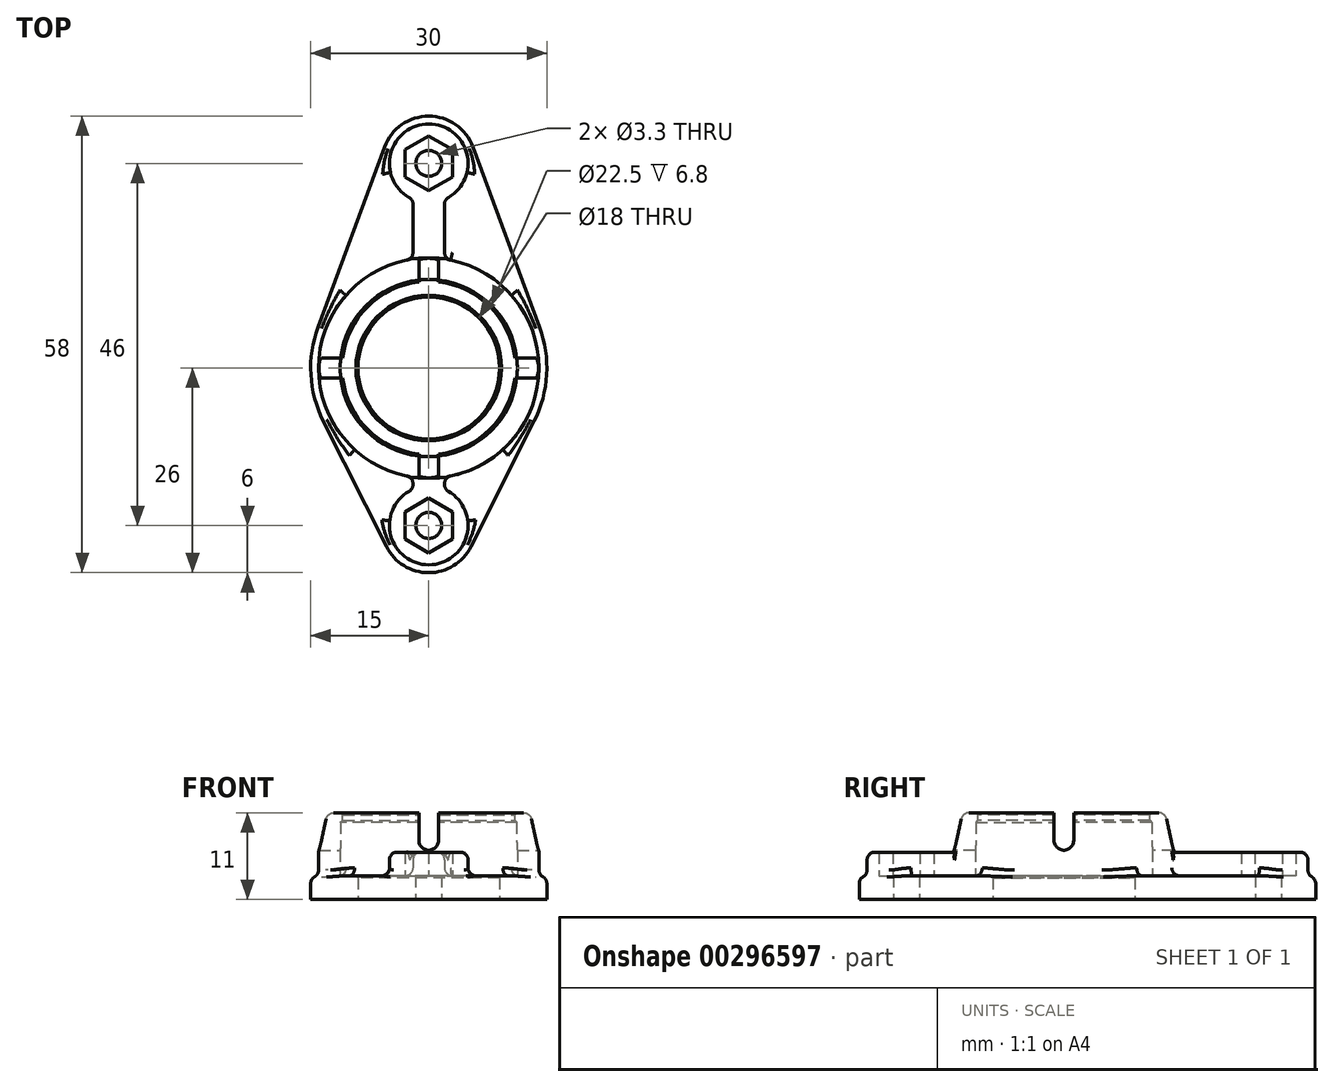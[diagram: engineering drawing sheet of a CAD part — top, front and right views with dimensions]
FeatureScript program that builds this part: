
annotation { "Feature Type Name" : "Feature", "Feature Type Description" : "" }
export const myFeature = defineFeature(function(context is Context, id is Id, definition is map)
    precondition{}
    {
        {
            var Q0;
            Q0=qCreatedBy(makeId("Top.planeOp"),FACE);
            var sketch = newSketch(context, id + "F0", { "sketchPlane" : qUnion([Q0])});
            skCircle(sketch, "E0", {"center": v(0, 0) * mm, "radius": 9 * mm});
            skArc(sketch, "E1", {"start": v(-14.07, 5.2) * mm, "mid": v(-14.98, -0.85) * mm, "end": v(-13.4, -6.75) * mm});
            skLineSegment(sketch, "E2", {"start": v(0, 0) * mm, "end": v(0, -20) * mm, "construction": true});
            skCircle(sketch, "E3", {"center": v(0, -20) * mm, "radius": 1.65 * mm});
            skLineSegment(sketch, "E4", {"start": v(0, 0) * mm, "end": v(0, 26) * mm, "construction": true});
            skCircle(sketch, "E5", {"center": v(0, 26) * mm, "radius": 1.65 * mm});
            skArc(sketch, "E6", {"start": v(5.63, 28.08) * mm, "mid": v(0, 32) * mm, "end": v(-5.63, 28.08) * mm});
            skArc(sketch, "E7", {"start": v(-5.36, -22.7) * mm, "mid": v(0, -26) * mm, "end": v(5.36, -22.7) * mm});
            skLineSegment(sketch, "E8", {"start": v(-5.63, 28.08) * mm, "end": v(-14.07, 5.2) * mm});
            skLineSegment(sketch, "E9", {"start": v(-13.4, -6.75) * mm, "end": v(-5.36, -22.7) * mm});
            skLineSegment(sketch, "E10", {"start": v(5.36, -22.7) * mm, "end": v(13.4, -6.75) * mm});
            skLineSegment(sketch, "E11", {"start": v(5.63, 28.08) * mm, "end": v(14.07, 5.2) * mm});
            skArc(sketch, "E12.trimOffspring", {"start": v(13.4, -6.75) * mm, "mid": v(14.98, -0.85) * mm, "end": v(14.07, 5.2) * mm});
            skSolve(sketch);
        }
        {
            var Q0;
            Q0=qSketchRegion(id+"F0",true);
            extrude(context, id + "F1", {"entities" : qUnion([Q0]), "depth" : 3 * mm});
        }
        {
            var Q0;
            Q0=makeQuery(id+"F1.opExtrude","CAP_FACE",FACE,{"disambiguationData":[OSD([sQuery(id+"F0.wireOp",EDGE,"E0"),sQuery(id+"F0.wireOp",EDGE,"E1"),sQuery(id+"F0.wireOp",EDGE,"E3"),sQuery(id+"F0.wireOp",EDGE,"E5"),sQuery(id+"F0.wireOp",EDGE,"E6"),sQuery(id+"F0.wireOp",EDGE,"E7"),sQuery(id+"F0.wireOp",EDGE,"E8"),sQuery(id+"F0.wireOp",EDGE,"E9"),sQuery(id+"F0.wireOp",EDGE,"E10"),sQuery(id+"F0.wireOp",EDGE,"E11"),sQuery(id+"F0.wireOp",EDGE,"E12.trimOffspring")])],"isStart":false});
            var sketch = newSketch(context, id + "F2", { "sketchPlane" : qUnion([Q0])});
            skArc(sketch, "E13", {"start": v(2.5, 21.67) * mm, "mid": v(0, 31) * mm, "end": v(-2.5, 21.67) * mm});
            skArc(sketch, "E14", {"start": v(-2.5, -15.67) * mm, "mid": v(0, -25) * mm, "end": v(2.5, -15.67) * mm});
            skCircle(sketch, "E15", {"center": v(0, 0) * mm, "radius": 11.25 * mm});
            skArc(sketch, "E16", {"start": v(-2.8, 13.72) * mm, "mid": v(-14, 0) * mm, "end": v(-2.8, -13.72) * mm});
            skLineSegment(sketch, "E17", {"start": v(0, 26) * mm, "end": v(0, 0) * mm, "construction": true});
            skLineSegment(sketch, "E18", {"start": v(0, -20) * mm, "end": v(0, 0) * mm, "construction": true});
            skLineSegment(sketch, "E19.0", {"start": v(2, -14.8) * mm, "end": v(2, -14.7) * mm});
            skLineSegment(sketch, "E20.0", {"start": v(-2, -14.8) * mm, "end": v(-2, -14.7) * mm});
            skLineSegment(sketch, "E21.0", {"start": v(-2, 20.8) * mm, "end": v(-2, 14.7) * mm});
            skLineSegment(sketch, "E22.0", {"start": v(2, 20.8) * mm, "end": v(2, 14.7) * mm});
            skArc(sketch, "E23.trimOffspring", {"start": v(2.8, -13.72) * mm, "mid": v(14, 0) * mm, "end": v(2.8, 13.72) * mm});
            skPoint(sketch, "E24.visualSharp", {"position": v(2, 13.86) * mm});
            skArc(sketch, "E24.filletArc", {"start": v(2, 14.7) * mm, "mid": v(2.23, 14.06) * mm, "end": v(2.8, 13.72) * mm});
            skPoint(sketch, "E25.visualSharp", {"position": v(2, -13.86) * mm});
            skArc(sketch, "E25.filletArc", {"start": v(2.8, -13.72) * mm, "mid": v(2.23, -14.06) * mm, "end": v(2, -14.7) * mm});
            skPoint(sketch, "E26.visualSharp", {"position": v(2, -15.42) * mm});
            skArc(sketch, "E26.filletArc", {"start": v(2, -14.8) * mm, "mid": v(2.13, -15.3) * mm, "end": v(2.5, -15.67) * mm});
            skPoint(sketch, "E27.visualSharp", {"position": v(-2, -15.42) * mm});
            skArc(sketch, "E27.filletArc", {"start": v(-2.5, -15.67) * mm, "mid": v(-2.13, -15.3) * mm, "end": v(-2, -14.8) * mm});
            skPoint(sketch, "E28.visualSharp", {"position": v(-2, -13.86) * mm});
            skArc(sketch, "E28.filletArc", {"start": v(-2, -14.7) * mm, "mid": v(-2.23, -14.06) * mm, "end": v(-2.8, -13.72) * mm});
            skPoint(sketch, "E29.visualSharp", {"position": v(2, 21.42) * mm});
            skArc(sketch, "E29.filletArc", {"start": v(2.5, 21.67) * mm, "mid": v(2.13, 21.3) * mm, "end": v(2, 20.8) * mm});
            skPoint(sketch, "E30.visualSharp", {"position": v(-2, 21.42) * mm});
            skArc(sketch, "E30.filletArc", {"start": v(-2, 20.8) * mm, "mid": v(-2.13, 21.3) * mm, "end": v(-2.5, 21.67) * mm});
            skPoint(sketch, "E31.visualSharp", {"position": v(-2, 13.86) * mm});
            skArc(sketch, "E31.filletArc", {"start": v(-2.8, 13.72) * mm, "mid": v(-2.23, 14.06) * mm, "end": v(-2, 14.7) * mm});
            skCircle(sketch, "E32.cCircle", {"center": v(0, 26) * mm, "radius": 3 * mm, "construction": true});
            skLineSegment(sketch, "E32.0", {"start": v(3, 27.73) * mm, "end": v(3, 24.27) * mm});
            skLineSegment(sketch, "E32.1", {"start": v(3, 24.27) * mm, "end": v(0, 22.54) * mm});
            skLineSegment(sketch, "E32.2", {"start": v(0, 22.54) * mm, "end": v(-3, 24.27) * mm});
            skLineSegment(sketch, "E32.3", {"start": v(-3, 24.27) * mm, "end": v(-3, 27.73) * mm});
            skLineSegment(sketch, "E32.4", {"start": v(-3, 27.73) * mm, "end": v(0, 29.46) * mm});
            skLineSegment(sketch, "E32.5", {"start": v(0, 29.46) * mm, "end": v(3, 27.73) * mm});
            skPoint(sketch, "E32.0.midPoint", {"position": v(3, 26) * mm});
            skCircle(sketch, "E33.cCircle", {"center": v(0, -20) * mm, "radius": 3 * mm, "construction": true});
            skLineSegment(sketch, "E33.0", {"start": v(3, -18.27) * mm, "end": v(3, -21.73) * mm});
            skLineSegment(sketch, "E33.1", {"start": v(3, -21.73) * mm, "end": v(0, -23.46) * mm});
            skLineSegment(sketch, "E33.2", {"start": v(0, -23.46) * mm, "end": v(-3, -21.73) * mm});
            skLineSegment(sketch, "E33.3", {"start": v(-3, -21.73) * mm, "end": v(-3, -18.27) * mm});
            skLineSegment(sketch, "E33.4", {"start": v(-3, -18.27) * mm, "end": v(0, -16.54) * mm});
            skLineSegment(sketch, "E33.5", {"start": v(0, -16.54) * mm, "end": v(3, -18.27) * mm});
            skPoint(sketch, "E33.0.midPoint", {"position": v(3, -20) * mm});
            skSolve(sketch);
        }
        {
            var Q0;
            Q0=qSketchRegion(id+"F2",true);
            extrude(context, id + "F3", {"entities" : qUnion([Q0]), "operationType" : NewBodyOperationType.ADD, "depth" : 3 * mm});
        }
        {
            var Q0;
            Q0=makeQuery(id+"F3.opExtrude","CAP_FACE",FACE,{"disambiguationData":[OSD([sQuery(id+"F2.wireOp",EDGE,"ErkzImGW-wcGA-vscJ-pKRm-jUK9ljDqNzHm"),sQuery(id+"F2.wireOp",EDGE,"E13"),sQuery(id+"F2.wireOp",EDGE,"mcYN25WA-hLG2-lxEH-biPS-aZDlqV3Zxszz"),sQuery(id+"F2.wireOp",EDGE,"E14"),sQuery(id+"F2.wireOp",EDGE,"E15"),sQuery(id+"F2.wireOp",EDGE,"E16"),sQuery(id+"F2.wireOp",EDGE,"E19.0"),sQuery(id+"F2.wireOp",EDGE,"E20.0"),sQuery(id+"F2.wireOp",EDGE,"E21.0"),sQuery(id+"F2.wireOp",EDGE,"E22.0"),sQuery(id+"F2.wireOp",EDGE,"E23.trimOffspring"),sQuery(id+"F2.wireOp",EDGE,"E24.filletArc"),sQuery(id+"F2.wireOp",EDGE,"E25.filletArc"),sQuery(id+"F2.wireOp",EDGE,"E26.filletArc"),sQuery(id+"F2.wireOp",EDGE,"E27.filletArc"),sQuery(id+"F2.wireOp",EDGE,"E28.filletArc"),sQuery(id+"F2.wireOp",EDGE,"E29.filletArc"),sQuery(id+"F2.wireOp",EDGE,"E30.filletArc"),sQuery(id+"F2.wireOp",EDGE,"E31.filletArc")])],"isStart":false});
            var sketch = newSketch(context, id + "F4", { "sketchPlane" : qUnion([Q0])});
            skCircle(sketch, "E34", {"center": v(0, 0) * mm, "radius": 14 * mm});
            skSolve(sketch);
        }
        {
            var Q0;
            Q0=qSketchRegion(id+"F4",true);
            extrude(context, id + "F5", {"entities" : qUnion([Q0]), "operationType" : NewBodyOperationType.ADD, "depth" : 5 * mm, "hasDraft" : true, "draftAngle" : 12 * degree, "draftPullDirection" : true});
        }
        {
            var Q0;
            Q0=makeQuery(id+"F5.opExtrude","CAP_FACE",FACE,{"disambiguationData":[OSD([sQuery(id+"F4.wireOp",EDGE,"E34")])],"isStart":false});
            var sketch = newSketch(context, id + "F6", { "sketchPlane" : qUnion([Q0])});
            skCircle(sketch, "E35", {"center": v(0, 0) * mm, "radius": 11.25 * mm});
            skSolve(sketch);
        }
        {
            var Q0;
            Q0=qSketchRegion(id+"F6",true);
            extrude(context, id + "F7", {"entities" : qUnion([Q0]), "operationType" : NewBodyOperationType.REMOVE, "oppositeDirection" : true, "depth" : 6 * mm});
        }
        {
            var Q0;
            Q0=makeQuery(id+"F5.opExtrude","CAP_FACE",FACE,{"disambiguationData":[OSD([sQuery(id+"F4.wireOp",EDGE,"E34")])],"isStart":false});
            var sketch = newSketch(context, id + "F8", { "sketchPlane" : qUnion([Q0])});
            skCircle(sketch, "E36", {"center": v(0, 0) * mm, "radius": 12.5 * mm});
            skCircle(sketch, "E37", {"center": v(0, 0) * mm, "radius": 11 * mm});
            skSolve(sketch);
        }
        {
            var Q0;
            Q0=qSketchRegion(id+"F8",true);
            extrude(context, id + "F9", {"entities" : qUnion([Q0]), "operationType" : NewBodyOperationType.ADD, "oppositeDirection" : true, "depth" : 1.2 * mm});
        }
        {
            var Q0;
            Q0=makeQuery(id+"F9.opExtrude","CAP_EDGE",EDGE,{"disambiguationData":[OSD([sQuery(id+"F8.wireOp",EDGE,"E37")])],"isStart":false});
            var Q1;
            Q1=makeQuery(id+"F9.opExtrude","CAP_EDGE",EDGE,{"disambiguationData":[OSD([sQuery(id+"F8.wireOp",EDGE,"E37")])],"isStart":true});
            var Q2;
            Q2=makeQuery(id+"F1.opExtrude","CAP_EDGE",EDGE,{"disambiguationData":[OSD([sQuery(id+"F0.wireOp",EDGE,"E0")])],"isStart":false});
            chamfer(context, id + "F10", {"entities" : qUnion([Q0, Q1, Q2]), "width" : 0.25 * mm, "tangentPropagation" : true});
        }
        {
            var Q0;
            Q0=qCreatedBy(makeId("Front.planeOp"),FACE);
            var sketch = newSketch(context, id + "F11", { "sketchPlane" : qUnion([Q0])});
            skLineSegment(sketch, "E38", {"start": v(0, 0) * mm, "end": v(0, 7.5) * mm, "construction": true});
            skArc(sketch, "E39", {"start": v(-1.25, 7.5) * mm, "mid": v(0, 6.25) * mm, "end": v(1.25, 7.5) * mm});
            skLineSegment(sketch, "E40", {"start": v(1.25, 7.5) * mm, "end": v(1.25, 12.5) * mm});
            skLineSegment(sketch, "E41", {"start": v(-1.25, 7.5) * mm, "end": v(-1.25, 12.5) * mm});
            skLineSegment(sketch, "E42", {"start": v(-1.25, 12.5) * mm, "end": v(1.25, 12.5) * mm});
            skSolve(sketch);
        }
        {
            var Q0;
            Q0=qSketchRegion(id+"F11",true);
            extrude(context, id + "F12", {"entities" : qUnion([Q0]), "operationType" : NewBodyOperationType.REMOVE, "endBound" : BoundingType.SYMMETRIC, "oppositeDirection" : true, "depth" : 30 * mm});
        }
        {
            var Q0;
            Q0=qCreatedBy(makeId("Right.planeOp"),FACE);
            var sketch = newSketch(context, id + "F13", { "sketchPlane" : qUnion([Q0])});
            skLineSegment(sketch, "E43", {"start": v(0, 0) * mm, "end": v(0, 7.5) * mm, "construction": true});
            skArc(sketch, "E44", {"start": v(-1.25, 7.5) * mm, "mid": v(0, 6.25) * mm, "end": v(1.25, 7.5) * mm});
            skLineSegment(sketch, "E45", {"start": v(1.25, 7.5) * mm, "end": v(1.25, 12.5) * mm});
            skLineSegment(sketch, "E46", {"start": v(-1.25, 7.5) * mm, "end": v(-1.25, 12.5) * mm});
            skLineSegment(sketch, "E47", {"start": v(-1.25, 12.5) * mm, "end": v(1.25, 12.5) * mm});
            skSolve(sketch);
        }
        {
            var Q0;
            Q0=qSketchRegion(id+"F13",true);
            extrude(context, id + "F14", {"entities" : qUnion([Q0]), "operationType" : NewBodyOperationType.REMOVE, "endBound" : BoundingType.SYMMETRIC, "oppositeDirection" : true, "depth" : 30 * mm});
        }
        {
            var Q0;
            Q0=makeQuery(id+"F1.opExtrude","CAP_EDGE",EDGE,{"disambiguationData":[OSD([sQuery(id+"F0.wireOp",EDGE,"E10")])],"isStart":false});
            var Q1;
            Q1=makeQuery(id+"F3.opExtrude","CAP_EDGE",EDGE,{"disambiguationData":[OSD([sQuery(id+"F2.wireOp",EDGE,"E14")])],"isStart":false});
            var Q2;
            {var subQ0=makeQuery(id+"F12.opExtrude","SWEPT_FACE",FACE,{"disambiguationData":[OSD([sQuery(id+"F11.wireOp",EDGE,"E40")])]});var subQ2=sQuery(id+"F4.wireOp",EDGE,"E34");Q2=makeQuery(id+"F14.boolean.opBoolean","SPLIT",EDGE,{"disambiguationData":[TD([makeQuery(id+"F12.boolean.opBoolean","COPY",FACE,{"disambiguationData":[OD(0.0)],"derivedFrom":subQ0})])],"derivedFrom":makeQuery(id+"F12.boolean.opBoolean","SPLIT",EDGE,{"disambiguationData":[TD([subQ0])],"derivedFrom":makeQuery(id+"F5.opExtrude","CAP_EDGE",EDGE,{"disambiguationData":[OSD([subQ2])],"isStart":false})})});}
            var Q3;
            {var subQ0=makeQuery(id+"F12.opExtrude","SWEPT_FACE",FACE,{"disambiguationData":[OSD([sQuery(id+"F11.wireOp",EDGE,"E40")])]});var subQ1=sQuery(id+"F4.wireOp",EDGE,"E34");Q3=makeQuery(id+"F14.boolean.opBoolean","SPLIT",EDGE,{"disambiguationData":[TD([makeQuery(id+"F12.boolean.opBoolean","COPY",FACE,{"disambiguationData":[OD(1.0)],"derivedFrom":subQ0})])],"derivedFrom":makeQuery(id+"F12.boolean.opBoolean","SPLIT",EDGE,{"disambiguationData":[TD([subQ0])],"derivedFrom":makeQuery(id+"F5.opExtrude","CAP_EDGE",EDGE,{"disambiguationData":[OSD([subQ1])],"isStart":false})})});}
            var Q4;
            Q4=makeQuery(id+"F3.opExtrude","CAP_EDGE",EDGE,{"disambiguationData":[OSD([sQuery(id+"F2.wireOp",EDGE,"E22.0")])],"isStart":false});
            var Q5;
            {var subQ0=makeQuery(id+"F12.opExtrude","SWEPT_FACE",FACE,{"disambiguationData":[OSD([sQuery(id+"F11.wireOp",EDGE,"E41")])]});var subQ2=sQuery(id+"F4.wireOp",EDGE,"E34");Q5=makeQuery(id+"F14.boolean.opBoolean","SPLIT",EDGE,{"disambiguationData":[TD([makeQuery(id+"F12.boolean.opBoolean","COPY",FACE,{"disambiguationData":[OD(0.0)],"derivedFrom":subQ0})])],"derivedFrom":makeQuery(id+"F12.boolean.opBoolean","SPLIT",EDGE,{"disambiguationData":[TD([subQ0])],"derivedFrom":makeQuery(id+"F5.opExtrude","CAP_EDGE",EDGE,{"disambiguationData":[OSD([subQ2])],"isStart":false})})});}
            var Q6;
            {var subQ1=sQuery(id+"F4.wireOp",EDGE,"E34");var subQ3=makeQuery(id+"F12.opExtrude","SWEPT_FACE",FACE,{"disambiguationData":[OSD([sQuery(id+"F11.wireOp",EDGE,"E41")])]});Q6=makeQuery(id+"F14.boolean.opBoolean","SPLIT",EDGE,{"disambiguationData":[TD([makeQuery(id+"F12.boolean.opBoolean","COPY",FACE,{"disambiguationData":[OD(1.0)],"derivedFrom":subQ3})])],"derivedFrom":makeQuery(id+"F12.boolean.opBoolean","SPLIT",EDGE,{"disambiguationData":[TD([subQ3])],"derivedFrom":makeQuery(id+"F5.opExtrude","CAP_EDGE",EDGE,{"disambiguationData":[OSD([subQ1])],"isStart":false})})});}
            fillet(context, id + "F15", {"entities" : qUnion([Q0, Q1, Q2, Q3, Q4, Q5, Q6]), "radius" : 1 * mm, "tangentPropagation" : true, "allowEdgeOverflow" : false});
        }
        {
            var Q0;
            Q0=makeQuery(id+"F3.opExtrude","CAP_EDGE",EDGE,{"disambiguationData":[OSD([sQuery(id+"F2.wireOp",EDGE,"E14")])],"isStart":true});
            fillet(context, id + "F16", {"entities" : qUnion([Q0]), "radius" : 1 * mm, "tangentPropagation" : true, "allowEdgeOverflow" : false});
        }
    });
